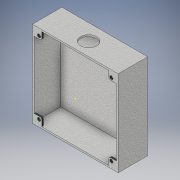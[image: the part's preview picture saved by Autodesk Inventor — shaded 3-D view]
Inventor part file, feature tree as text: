
AUTODESK INVENTOR PART (.ipt)
format: ipt  version: 2018 (Build 220112000, 112)  size: 206,848 bytes
history: native  units: in
note: dims shown in document units (in); Inventor stores cm internally (conversion verified against a paired STEP export)
features: sketch x5, extrude x4, fillet x1
ambient origin geometry x8: Origin, YZ Plane, XZ Plane, XY Plane, X Axis, Y Axis, Z Axis, Center Point
bodies: Solid1 (feature_tree)
feature tree (10):
  extrude  "Extrusion1"  Depth=4.0in
  extrude  "Extrusion2"  Depth=0.08in
  extrude  "Extrusion3"  Depth=1.25in TaperAngle=0.0deg
  sketch  "Sketch6"  dims[d9=0.75in d10=1.0in d11=0.0in d12=3.375in]
  extrude  "Extrusion4"  Depth=1.0in TaperAngle=0.0deg
  fillet  "Fillet1"  Radius=3.375in
  sketch  "Sketch1"  dims[d0=4.0in d1=4.0in]
  sketch  "Sketch2"  dims[d2=0.125in d3=0.0in d4=0.08in]
  sketch  "Sketch5"  dims[d5=0.08in d6=1.25in d7=0.0in]
  sketch  "Sketch7"  dims[d13=0.1575in d14=0.1575in d16=3.375in d17=1.6875in d18=1.6875in d19=0.1575in d20=0.1575in d21=1.6875in d22=1.6875in d23=3.375in d24=1.6875in d25=1.6875in d26=0.125in d27=0.125in d28=0.125in d29=0.125in d30=0.125in d31=0.125in d32=0.125in d33=0.125in d34=0.0787in d35=0.0in d36=0.0787in]
